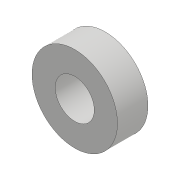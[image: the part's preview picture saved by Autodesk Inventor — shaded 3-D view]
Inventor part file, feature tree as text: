
AUTODESK INVENTOR PART (.ipt)
format: ipt  version: 2018 (Build 220112000, 112)  size: 82,432 bytes
history: native  units: mm
features: extrude x1, sketch x1
ambient origin geometry x8: Origin, YZ Plane, XZ Plane, XY Plane, X Axis, Y Axis, Z Axis, Center Point
bodies: Solid1 (feature_tree)
feature tree (2):
  extrude  "Extrusion1"  Depth=2.5mm
  sketch  "Sketch1"  dims[d0=7.0mm d1=3.2mm d2=2.5mm d3=0.0mm]
